FCSTD DOCUMENT  (FreeCAD 0.19R24291 (Git))
Label: keyboard-pc
License: All rights reserved
LicenseURL: http://en.wikipedia.org/wiki/All_rights_reserved
objects: Sketcher::SketchObject×1, PartDesign::Body×1
note: 2 computed .brp shape members not serialized (recipe doc carries the construction recipe); baked Part::Feature solids carry a one-line shape summary decoded from their .brp

FEATURE [Sketcher::SketchObject] Sketch
  FullyConstrained = false
  MapMode = 5
  Support = -> [XY_Plane]
  sketch-geometry (91):
    g0: LineSegment StartX=-178.5 StartY=64 StartZ=0 EndX=178.5 EndY=64 EndZ=0
    g1: LineSegment StartX=178.5 StartY=64 StartZ=0 EndX=178.5 EndY=-64 EndZ=0
    g2: LineSegment StartX=178.5 StartY=-64 StartZ=0 EndX=-178.5 EndY=-64 EndZ=0
    g3: LineSegment StartX=-178.5 StartY=-64 StartZ=0 EndX=-178.5 EndY=64 EndZ=0
    g4: Circle CenterX=-171.5 CenterY=56 CenterZ=0 NormalX=0 NormalY=0 NormalZ=1 AngleXU=0 Radius=1
    g5: Circle CenterX=-165.5 CenterY=58 CenterZ=0 NormalX=0 NormalY=0 NormalZ=1 AngleXU=0 Radius=1
    g6: Circle CenterX=-157.5 CenterY=58 CenterZ=0 NormalX=0 NormalY=0 NormalZ=1 AngleXU=0 Radius=1
    g7: Circle CenterX=-165.5 CenterY=-9 CenterZ=0 NormalX=0 NormalY=0 NormalZ=1 AngleXU=0 Radius=1
    g8: Circle CenterX=-166.5 CenterY=-35 CenterZ=0 NormalX=0 NormalY=0 NormalZ=1 AngleXU=0 Radius=1
    g9: Circle CenterX=0 CenterY=59 CenterZ=0 NormalX=0 NormalY=0 NormalZ=1 AngleXU=0 Radius=1
    g10: Circle CenterX=146.5 CenterY=60 CenterZ=0 NormalX=0 NormalY=0 NormalZ=1 AngleXU=0 Radius=1
    g11: Circle CenterX=161.5 CenterY=43 CenterZ=0 NormalX=0 NormalY=0 NormalZ=1 AngleXU=0 Radius=1
    g12: Circle CenterX=161.5 CenterY=-4 CenterZ=0 NormalX=0 NormalY=0 NormalZ=1 AngleXU=0 Radius=1
    g13: Circle CenterX=166.5 CenterY=-35 CenterZ=0 NormalX=0 NormalY=0 NormalZ=1 AngleXU=0 Radius=1
    g14: Circle CenterX=127.5 CenterY=52 CenterZ=0 NormalX=0 NormalY=0 NormalZ=1 AngleXU=0 Radius=1
    g15: Circle CenterX=127.5 CenterY=43 CenterZ=0 NormalX=0 NormalY=0 NormalZ=1 AngleXU=0 Radius=1
    g16: Circle CenterX=127.5 CenterY=3 CenterZ=0 NormalX=0 NormalY=0 NormalZ=1 AngleXU=0 Radius=1
    g17: Circle CenterX=87.5 CenterY=43 CenterZ=0 NormalX=0 NormalY=0 NormalZ=1 AngleXU=0 Radius=1
    g18: Circle CenterX=87.5 CenterY=3 CenterZ=0 NormalX=0 NormalY=0 NormalZ=1 AngleXU=0 Radius=1
    g19: Circle CenterX=108.5 CenterY=-61 CenterZ=0 NormalX=0 NormalY=0 NormalZ=1 AngleXU=0 Radius=1
    g20: Circle CenterX=68.5 CenterY=-61 CenterZ=0 NormalX=0 NormalY=0 NormalZ=1 AngleXU=0 Radius=1
    g21: Circle CenterX=0 CenterY=-61 CenterZ=0 NormalX=0 NormalY=0 NormalZ=1 AngleXU=0 Radius=0
    g22: Circle CenterX=0 CenterY=-61 CenterZ=0 NormalX=0 NormalY=0 NormalZ=1 AngleXU=0 Radius=1
    g23: LineSegment StartX=14.4557 StartY=-56 StartZ=0 EndX=140.456 EndY=-56 EndZ=0
    g24: LineSegment StartX=140.456 StartY=-56 StartZ=0 EndX=140.456 EndY=-58 EndZ=0
    g25: LineSegment StartX=140.456 StartY=-58 StartZ=0 EndX=14.4557 EndY=-58 EndZ=0
    g26: LineSegment StartX=14.4557 StartY=-58 StartZ=0 EndX=14.4557 EndY=-56 EndZ=0
    g27: LineSegment StartX=14.4557 StartY=-48 StartZ=0 EndX=140.456 EndY=-48 EndZ=0
    g28: LineSegment StartX=140.456 StartY=-48 StartZ=0 EndX=140.456 EndY=-50 EndZ=0
    g29: LineSegment StartX=140.456 StartY=-50 StartZ=0 EndX=14.4557 EndY=-50 EndZ=0
    g30: LineSegment StartX=14.4557 StartY=-50 StartZ=0 EndX=14.4557 EndY=-48 EndZ=0
    g31: LineSegment StartX=27.7905 StartY=43 StartZ=0 EndX=29.7905 EndY=43 EndZ=0
    g32: LineSegment StartX=29.7905 StartY=43 StartZ=0 EndX=29.7905 EndY=3 EndZ=0
    g33: LineSegment StartX=29.7905 StartY=3 StartZ=0 EndX=27.7905 EndY=3 EndZ=0
    g34: LineSegment StartX=27.7905 StartY=3 StartZ=0 EndX=27.7905 EndY=43 EndZ=0
    g35: LineSegment StartX=33.7905 StartY=43 StartZ=0 EndX=35.7905 EndY=43 EndZ=0
    g36: LineSegment StartX=35.7905 StartY=43 StartZ=0 EndX=35.7905 EndY=3 EndZ=0
    g37: LineSegment StartX=35.7905 StartY=3 StartZ=0 EndX=33.7905 EndY=3 EndZ=0
    g38: LineSegment StartX=33.7905 StartY=3 StartZ=0 EndX=33.7905 EndY=43 EndZ=0
    g39: LineSegment StartX=39.7905 StartY=43 StartZ=0 EndX=41.7905 EndY=43 EndZ=0
    g40: LineSegment StartX=41.7905 StartY=43 StartZ=0 EndX=41.7905 EndY=3 EndZ=0
    g41: LineSegment StartX=41.7905 StartY=3 StartZ=0 EndX=39.7905 EndY=3 EndZ=0
    g42: LineSegment StartX=39.7905 StartY=3 StartZ=0 EndX=39.7905 EndY=43 EndZ=0
    g43: LineSegment StartX=45.7905 StartY=43 StartZ=0 EndX=47.7905 EndY=43 EndZ=0
    g44: LineSegment StartX=47.7905 StartY=43 StartZ=0 EndX=47.7905 EndY=3 EndZ=0
    g45: LineSegment StartX=47.7905 StartY=3 StartZ=0 EndX=45.7905 EndY=3 EndZ=0
    g46: LineSegment StartX=45.7905 StartY=3 StartZ=0 EndX=45.7905 EndY=43 EndZ=0
    g47: LineSegment StartX=51.7905 StartY=43 StartZ=0 EndX=53.7905 EndY=43 EndZ=0
    g48: LineSegment StartX=53.7905 StartY=43 StartZ=0 EndX=53.7905 EndY=3 EndZ=0
    g49: LineSegment StartX=53.7905 StartY=3 StartZ=0 EndX=51.7905 EndY=3 EndZ=0
    g50: LineSegment StartX=51.7905 StartY=3 StartZ=0 EndX=51.7905 EndY=43 EndZ=0
    g51: LineSegment StartX=57.7905 StartY=43 StartZ=0 EndX=59.7905 EndY=43 EndZ=0
    g52: LineSegment StartX=59.7905 StartY=43 StartZ=0 EndX=59.7905 EndY=3 EndZ=0
    g53: LineSegment StartX=59.7905 StartY=3 StartZ=0 EndX=57.7905 EndY=3 EndZ=0
    g54: LineSegment StartX=57.7905 StartY=3 StartZ=0 EndX=57.7905 EndY=43 EndZ=0
    g55: LineSegment StartX=63.7905 StartY=43 StartZ=0 EndX=65.7905 EndY=43 EndZ=0
    g56: LineSegment StartX=65.7905 StartY=43 StartZ=0 EndX=65.7905 EndY=3 EndZ=0
    g57: LineSegment StartX=65.7905 StartY=3 StartZ=0 EndX=63.7905 EndY=3 EndZ=0
    g58: LineSegment StartX=63.7905 StartY=3 StartZ=0 EndX=63.7905 EndY=43 EndZ=0
    g59: LineSegment StartX=69.7905 StartY=43 StartZ=0 EndX=71.7905 EndY=43 EndZ=0
    g60: LineSegment StartX=71.7905 StartY=43 StartZ=0 EndX=71.7905 EndY=3 EndZ=0
    g61: LineSegment StartX=71.7905 StartY=3 StartZ=0 EndX=69.7905 EndY=3 EndZ=0
    g62: LineSegment StartX=69.7905 StartY=3 StartZ=0 EndX=69.7905 EndY=43 EndZ=0
    g63: LineSegment StartX=91.5 StartY=43 StartZ=0 EndX=93.5 EndY=43 EndZ=0
    g64: LineSegment StartX=93.5 StartY=43 StartZ=0 EndX=93.5 EndY=3 EndZ=0
    g65: LineSegment StartX=93.5 StartY=3 StartZ=0 EndX=91.5 EndY=3 EndZ=0
    g66: LineSegment StartX=91.5 StartY=3 StartZ=0 EndX=91.5 EndY=43 EndZ=0
    g67: LineSegment StartX=97.5 StartY=43 StartZ=0 EndX=99.5 EndY=43 EndZ=0
    g68: LineSegment StartX=99.5 StartY=43 StartZ=0 EndX=99.5 EndY=3 EndZ=0
    g69: LineSegment StartX=99.5 StartY=3 StartZ=0 EndX=97.5 EndY=3 EndZ=0
    g70: LineSegment StartX=97.5 StartY=3 StartZ=0 EndX=97.5 EndY=43 EndZ=0
    g71: LineSegment StartX=103.5 StartY=43 StartZ=0 EndX=105.5 EndY=43 EndZ=0
    g72: LineSegment StartX=105.5 StartY=43 StartZ=0 EndX=105.5 EndY=3 EndZ=0
    g73: LineSegment StartX=105.5 StartY=3 StartZ=0 EndX=103.5 EndY=3 EndZ=0
    g74: LineSegment StartX=103.5 StartY=3 StartZ=0 EndX=103.5 EndY=43 EndZ=0
    g75: LineSegment StartX=109.5 StartY=43 StartZ=0 EndX=111.5 EndY=43 EndZ=0
    g76: LineSegment StartX=111.5 StartY=43 StartZ=0 EndX=111.5 EndY=3 EndZ=0
    g77: LineSegment StartX=111.5 StartY=3 StartZ=0 EndX=109.5 EndY=3 EndZ=0
    g78: LineSegment StartX=109.5 StartY=3 StartZ=0 EndX=109.5 EndY=43 EndZ=0
    g79: LineSegment StartX=115.5 StartY=43 StartZ=0 EndX=117.5 EndY=43 EndZ=0
    g80: LineSegment StartX=117.5 StartY=43 StartZ=0 EndX=117.5 EndY=3 EndZ=0
    g81: LineSegment StartX=117.5 StartY=3 StartZ=0 EndX=115.5 EndY=3 EndZ=0
    g82: LineSegment StartX=115.5 StartY=3 StartZ=0 EndX=115.5 EndY=43 EndZ=0
    g83: LineSegment StartX=121.5 StartY=43 StartZ=0 EndX=123.5 EndY=43 EndZ=0
    g84: LineSegment StartX=123.5 StartY=43 StartZ=0 EndX=123.5 EndY=3 EndZ=0
    g85: LineSegment StartX=123.5 StartY=3 StartZ=0 EndX=121.5 EndY=3 EndZ=0
    g86: LineSegment StartX=121.5 StartY=3 StartZ=0 EndX=121.5 EndY=43 EndZ=0
    g87: LineSegment StartX=14.4557 StartY=-40 StartZ=0 EndX=140.456 EndY=-40 EndZ=0
    g88: LineSegment StartX=140.456 StartY=-40 StartZ=0 EndX=140.456 EndY=-42 EndZ=0
    g89: LineSegment StartX=140.456 StartY=-42 StartZ=0 EndX=14.4557 EndY=-42 EndZ=0
    g90: LineSegment StartX=14.4557 StartY=-42 StartZ=0 EndX=14.4557 EndY=-40 EndZ=0
  constraints (267):
    c: Coincident(g0,g1)
    c: Coincident(g1,g2)
    c: Coincident(g2,g3)
    c: Coincident(g3,g0)
    c: Horizontal(g2)
    c: Vertical(g1)
    c: Symmetric(g0,g2,g-1)
    c: Symmetric(g0,g0,g-2)
    c: DistanceX(g0,g0) = 357
    c: DistanceY(g3,g3) = 128
    c: Radius(g4) = 1
    c: DistanceX(g0,g4) = 7
    c: DistanceY(g4,g0) = 8
    c: Radius(g5) = 1
    c: DistanceY(g5,g0) = 6
    c: DistanceX(g4,g5) = 6
    c: Radius(g6) = 1
    c: DistanceX(g5,g6) = 8
    c: DistanceY(g6,g0) = 6
    c: Radius(g7) = 1
    c: DistanceY(g7,g5) = 67
    c: Vertical(g7,g5)
    c: Radius(g8) = 1
    c: DistanceY(g2,g8) = 29
    c: DistanceX(g2,g8) = 12
    c: Vertical(g9,g-1)
    c: DistanceY(g9,g0) = 5
    c: Radius(g9) = 1
    c: DistanceX(g10,g0) = 32
    c: DistanceY(g10,g0) = 4
    c: Radius(g10) = 1
    c: DistanceY(g11,g0) = 21
    c: DistanceX(g11,g0) = 17
    c: Radius(g11) = 1
    c: Vertical(g12,g11)
    c: DistanceY(g12,g11) = 47
    c: Radius(g12) = 1
    c: DistanceY(g1,g13) = 29
    c: DistanceX(g13,g1) = 12
    c: Radius(g13) = 1
    c: DistanceX(g14,g11) = 34
    c: DistanceY(g14,g0) = 12
    c: Radius(g14) = 1
    c: Horizontal(g15,g11)
    c: Vertical(g15,g14)
    c: Radius(g15) = 1
    c: Vertical(g16,g15)
    c: DistanceY(g16,g15) = 40
    c: Radius(g16) = 1
    c: Horizontal(g17,g15)
    c: DistanceX(g17,g15) = 40
    c: Radius(g17) = 1
    c: Radius(g18) = 1
    c: Horizontal(g18,g16)
    c: DistanceX(g18,g16) = 40
    c: DistanceX(g19,g1) = 70
    c: DistanceY(g1,g19) = 3
    c: Radius(g19) = 1
    c: Horizontal(g20,g19)
    c: DistanceX(g20,g19) = 40
    c: Radius(g20) = 1
    c: Coincident(g22,g21)
    c: Horizontal(g21,g20)
    c: Vertical(g21,g-1)
    c: Radius(g22) = 1
    c: Coincident(g23,g24)
    c: Coincident(g24,g25)
    c: Coincident(g25,g26)
    c: Coincident(g26,g23)
    c: Horizontal(g23)
    c: Horizontal(g25)
    c: Vertical(g24)
    c: Vertical(g26)
    c: DistanceX(g25,g24) = 126
    c: DistanceY(g24,g23) = 2
    c: DistanceY(g1,g24) = 6
    c: Coincident(g27,g28)
    c: Coincident(g28,g29)
    c: Coincident(g29,g30)
    c: Coincident(g30,g27)
    c: Horizontal(g27)
    c: Horizontal(g29)
    c: Vertical(g28)
    c: Vertical(g30)
    c: Vertical(g28,g23)
    c: Vertical(g23,g29)
    c: DistanceY(g28,g27) = 2
    c: DistanceY(g23,g28) = 6
    c: Coincident(g31,g32)
    c: Coincident(g32,g33)
    c: Coincident(g33,g34)
    c: Coincident(g34,g31)
    c: Horizontal(g31)
    c: Horizontal(g33)
    c: Vertical(g32)
    c: Vertical(g34)
    c: DistanceX(g33,g32) = 2
    c: DistanceY(g32,g31) = 40
    c: Horizontal(g31,g17)
    c: Coincident(g35,g36)
    c: Coincident(g36,g37)
    c: Coincident(g37,g38)
    c: Coincident(g38,g35)
    c: Horizontal(g35)
    c: Horizontal(g37)
    c: Vertical(g36)
    c: Vertical(g38)
    c: DistanceX(g35,g35) = 2
    c: DistanceY(g36,g35) = 40
    c: Horizontal(g35,g31)
    c: DistanceX(g31,g35) = 4
    c: Coincident(g39,g40)
    c: Coincident(g40,g41)
    c: Coincident(g41,g42)
    c: Coincident(g42,g39)
    c: Horizontal(g39)
    c: Horizontal(g41)
    c: Vertical(g40)
    c: Vertical(g42)
    c: DistanceX(g41,g40) = 2
    c: DistanceY(g40,g39) = 40
    c: Coincident(g43,g44)
    c: Coincident(g44,g45)
    c: Coincident(g45,g46)
    c: Coincident(g46,g43)
    c: Horizontal(g43)
    c: Horizontal(g45)
    c: Vertical(g44)
    c: Vertical(g46)
    c: Equal(g35,g43) = 2
    c: DistanceY(g44,g43) = 40
    c: Horizontal(g43,g39)
    c: DistanceX(g39,g43) = 4
    c: DistanceX(g36,g41) = 4
    c: Horizontal(g36,g41)
    c: Coincident(g47,g48)
    c: Coincident(g48,g49)
    c: Coincident(g49,g50)
    c: Coincident(g50,g47)
    c: Horizontal(g47)
    c: Horizontal(g49)
    c: Vertical(g48)
    c: Vertical(g50)
    c: DistanceX(g49,g48) = 2
    c: DistanceY(g48,g47) = 40
    c: Coincident(g51,g52)
    c: Coincident(g52,g53)
    c: Coincident(g53,g54)
    c: Coincident(g54,g51)
    c: Horizontal(g51)
    c: Horizontal(g53)
    c: Vertical(g52)
    c: Vertical(g54)
    c: Equal(g35,g51) = 2
    c: DistanceY(g52,g51) = 40
    c: Horizontal(g51,g47)
    c: DistanceX(g47,g51) = 4
    c: Coincident(g55,g56)
    c: Coincident(g56,g57)
    c: Coincident(g57,g58)
    c: Coincident(g58,g55)
    c: Horizontal(g55)
    c: Horizontal(g57)
    c: Vertical(g56)
    c: Vertical(g58)
    c: DistanceX(g57,g56) = 2
    c: DistanceY(g56,g55) = 40
    c: Coincident(g59,g60)
    c: Coincident(g60,g61)
    c: Coincident(g61,g62)
    c: Coincident(g62,g59)
    c: Horizontal(g59)
    c: Horizontal(g61)
    c: Vertical(g60)
    c: Vertical(g62)
    c: Equal(g51,g59) = 2
    c: DistanceY(g60,g59) = 40
    c: Horizontal(g59,g55)
    c: DistanceX(g55,g59) = 4
    c: DistanceX(g52,g57) = 4
    c: Horizontal(g52,g57)
    c: Horizontal(g49,g44)
    c: DistanceX(g44,g49) = 4
    c: Coincident(g63,g64)
    c: Coincident(g64,g65)
    c: Coincident(g65,g66)
    c: Coincident(g66,g63)
    c: Horizontal(g63)
    c: Horizontal(g65)
    c: Vertical(g64)
    c: Vertical(g66)
    c: DistanceX(g65,g64) = 2
    c: DistanceY(g64,g63) = 40
    c: Coincident(g67,g68)
    c: Coincident(g68,g69)
    c: Coincident(g69,g70)
    c: Coincident(g70,g67)
    c: Horizontal(g67)
    c: Horizontal(g69)
    c: Vertical(g68)
    c: Vertical(g70)
    c: DistanceY(g68,g67) = 40
    c: Horizontal(g67,g63)
    c: DistanceX(g63,g67) = 4
    c: Coincident(g71,g72)
    c: Coincident(g72,g73)
    c: Coincident(g73,g74)
    c: Coincident(g74,g71)
    c: Horizontal(g71)
    c: Horizontal(g73)
    c: Vertical(g72)
    c: Vertical(g74)
    c: DistanceX(g73,g72) = 2
    c: DistanceY(g72,g71) = 40
    c: Coincident(g75,g76)
    c: Coincident(g76,g77)
    c: Coincident(g77,g78)
    c: Coincident(g78,g75)
    c: Horizontal(g75)
    c: Horizontal(g77)
    c: Vertical(g76)
    c: Vertical(g78)
    c: DistanceY(g76,g75) = 40
    c: Horizontal(g75,g71)
    c: DistanceX(g71,g75) = 4
    c: Coincident(g79,g80)
    c: Coincident(g80,g81)
    c: Coincident(g81,g82)
    c: Coincident(g82,g79)
    c: Horizontal(g79)
    c: Horizontal(g81)
    c: Vertical(g80)
    c: Vertical(g82)
    c: DistanceX(g81,g80) = 2
    c: DistanceY(g80,g79) = 40
    c: Coincident(g83,g84)
    c: Coincident(g84,g85)
    c: Coincident(g85,g86)
    c: Coincident(g86,g83)
    c: Horizontal(g83)
    c: Horizontal(g85)
    c: Vertical(g84)
    c: Vertical(g86)
    c: Equal(g75,g83) = 2
    c: DistanceY(g84,g83) = 40
    c: Horizontal(g83,g79)
    c: DistanceX(g79,g83) = 4
    c: DistanceX(g76,g81) = 4
    c: Horizontal(g76,g81)
    c: Horizontal(g73,g68)
    c: DistanceX(g68,g73) = 4
    c: Horizontal(g65,g18)
    c: DistanceX(g18,g65) = 4
    c: DistanceX(g69,g68) = 2
    c: DistanceX(g77,g76) = 2
    c: Coincident(g87,g88)
    c: Coincident(g88,g89)
    c: Coincident(g89,g90)
    c: Coincident(g90,g87)
    c: Horizontal(g87)
    c: Horizontal(g89)
    c: Vertical(g88)
    c: Vertical(g90)
    c: Vertical(g89,g27)
    c: DistanceY(g89,g87) = 2
    c: DistanceY(g27,g89) = 6
    c: Vertical(g88,g27)
FEATURE [PartDesign::Body] Body
  Group = -> [Sketch]
  Origin = -> Origin
